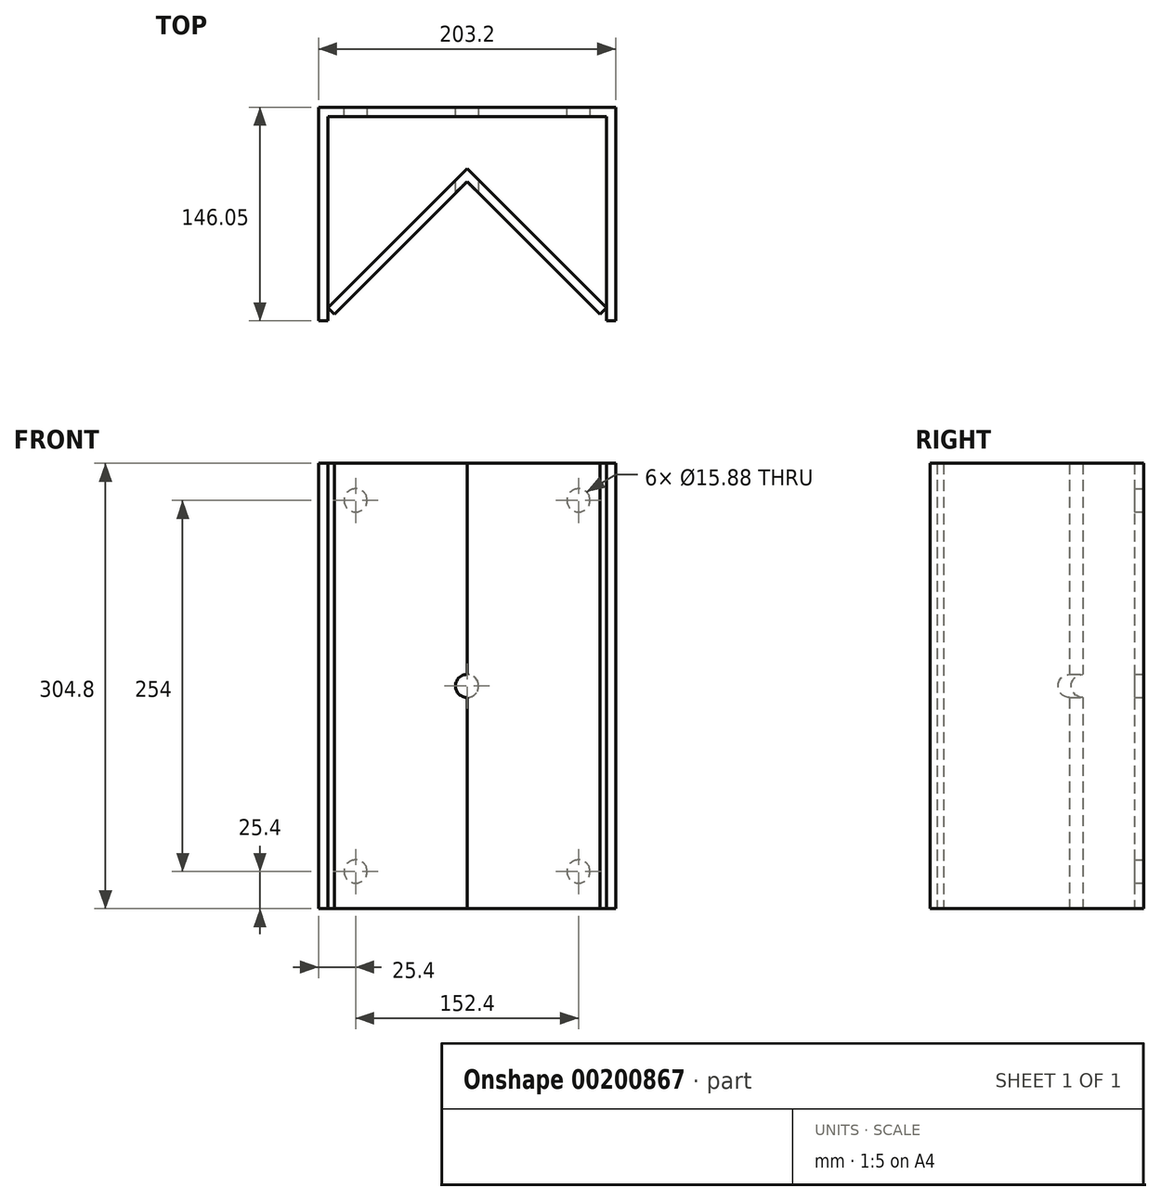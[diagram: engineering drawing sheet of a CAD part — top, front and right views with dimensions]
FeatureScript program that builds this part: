
annotation { "Feature Type Name" : "Feature", "Feature Type Description" : "" }
export const myFeature = defineFeature(function(context is Context, id is Id, definition is map)
    precondition{}
    {
        {
            var Q0;
            Q0=qCreatedBy(makeId("Top.planeOp"),FACE);
            var sketch = newSketch(context, id + "F0", { "sketchPlane" : qUnion([Q0])});
            skLineSegment(sketch, "E0", {"start": v(-95.25, 0) * mm, "end": v(95.25, 0) * mm});
            skLineSegment(sketch, "E1", {"start": v(95.25, 0) * mm, "end": v(95.25, -139.7) * mm});
            skLineSegment(sketch, "E2", {"start": v(95.25, -139.7) * mm, "end": v(101.6, -139.7) * mm});
            skLineSegment(sketch, "E3", {"start": v(101.6, -139.7) * mm, "end": v(101.6, 6.35) * mm});
            skLineSegment(sketch, "E4", {"start": v(101.6, 6.35) * mm, "end": v(-101.6, 6.35) * mm});
            skLineSegment(sketch, "E5", {"start": v(-101.6, 6.35) * mm, "end": v(-101.6, -139.7) * mm});
            skLineSegment(sketch, "E6", {"start": v(-101.6, -139.7) * mm, "end": v(-95.25, -139.7) * mm});
            skLineSegment(sketch, "E7", {"start": v(-95.25, -139.7) * mm, "end": v(-95.25, 0) * mm});
            skSolve(sketch);
        }
        {
            var Q0;
            Q0 = qSketchRegion(id + "F0", true);
            extrude(context, id + "F1", {"entities" : qUnion([Q0]), "depth" : 304.8 * mm});
        }
        {
            var Q0;
            Q0=qCreatedBy(makeId("Top.planeOp"),FACE);
            var sketch = newSketch(context, id + "F2", { "sketchPlane" : qUnion([Q0])});
            skLineSegment(sketch, "E8", {"start": v(-95.25, -139.7) * mm, "end": v(0, -44.45) * mm, "construction": true});
            skLineSegment(sketch, "E9", {"start": v(0, -44.45) * mm, "end": v(95.25, -139.7) * mm, "construction": true});
            skSolve(sketch);
        }
        {
            var Q0;
            Q0=qCreatedBy(makeId("Top.planeOp"),FACE);
            var sketch = newSketch(context, id + "F3", { "sketchPlane" : qUnion([Q0])});
            skLineSegment(sketch, "E10", {"start": v(-90.76, -135.2) * mm, "end": v(0, -44.45) * mm});
            skLineSegment(sketch, "E11", {"start": v(0, -44.45) * mm, "end": v(90.76, -135.2) * mm});
            skLineSegment(sketch, "E12", {"start": v(90.76, -135.2) * mm, "end": v(95.25, -130.72) * mm});
            skLineSegment(sketch, "E13", {"start": v(95.25, -130.72) * mm, "end": v(0, -35.47) * mm});
            skLineSegment(sketch, "E14", {"start": v(-95.25, -130.72) * mm, "end": v(-90.76, -135.2) * mm});
            skLineSegment(sketch, "E15", {"start": v(-95.25, -130.72) * mm, "end": v(0, -35.47) * mm});
            skSolve(sketch);
        }
        {
            var Q0;
            Q0 = qSketchRegion(id + "F3", true);
            var Q1;
            Q1=makeQuery(id+"F1.opExtrude","CAP_FACE",FACE,{"disambiguationData":[OSD([sQuery(id+"F0.wireOp",EDGE,"E0"),sQuery(id+"F0.wireOp",EDGE,"E1"),sQuery(id+"F0.wireOp",EDGE,"E2"),sQuery(id+"F0.wireOp",EDGE,"E3"),sQuery(id+"F0.wireOp",EDGE,"E4"),sQuery(id+"F0.wireOp",EDGE,"E5"),sQuery(id+"F0.wireOp",EDGE,"E6"),sQuery(id+"F0.wireOp",EDGE,"E7")])],"isStart":false});
            extrude(context, id + "F4", {"entities" : qUnion([Q0]), "endBound" : BoundingType.UP_TO_SURFACE, "endBoundEntityFace" : qUnion([Q1]), "depth" : 25.4 * mm});
        }
        {
            var Q0;
            Q0=makeQuery(id+"F1.opExtrude","SWEPT_FACE",FACE,{"disambiguationData":[OSD([sQuery(id+"F0.wireOp",EDGE,"E4")])]});
            var sketch = newSketch(context, id + "F5", { "sketchPlane" : qUnion([Q0])});
            skPoint(sketch, "E16", {"position": v(-76.2, 279.4) * mm});
            skPoint(sketch, "E17", {"position": v(76.2, 279.4) * mm});
            skPoint(sketch, "E18", {"position": v(-76.2, 25.4) * mm});
            skPoint(sketch, "E19", {"position": v(76.2, 25.4) * mm});
            skSolve(sketch);
        }
        {
            var Q0;
            Q0=sQuery(id+"F5.wireOp",VERTEX,"E16");
            var Q1;
            Q1=sQuery(id+"F5.wireOp",VERTEX,"E17");
            var Q2;
            Q2=sQuery(id+"F5.wireOp",VERTEX,"E18");
            var Q3;
            Q3=sQuery(id+"F5.wireOp",VERTEX,"E19");
            var Q4;
            Q4=makeQuery(id+"F1.opExtrude","SWEPT_BODY",BODY,{"disambiguationData":[OSD([sQuery(id+"F0.wireOp",EDGE,"E0"),sQuery(id+"F0.wireOp",EDGE,"E1"),sQuery(id+"F0.wireOp",EDGE,"E2"),sQuery(id+"F0.wireOp",EDGE,"E3"),sQuery(id+"F0.wireOp",EDGE,"E4"),sQuery(id+"F0.wireOp",EDGE,"E5"),sQuery(id+"F0.wireOp",EDGE,"E6"),sQuery(id+"F0.wireOp",EDGE,"E7")])]});
            var Q5;
            Q5=makeQuery(id+"F4.opExtrude","SWEPT_BODY",BODY,{"disambiguationData":[OSD([sQuery(id+"F3.wireOp",EDGE,"E10"),sQuery(id+"F3.wireOp",EDGE,"E11"),sQuery(id+"F3.wireOp",EDGE,"E12"),sQuery(id+"F3.wireOp",EDGE,"E13"),sQuery(id+"F3.wireOp",EDGE,"E14"),sQuery(id+"F3.wireOp",EDGE,"E15")])]});
            hole(context, id + "F6", {"style" : HoleStyle.SIMPLE, "endStyle" : HoleEndStyle.BLIND, "holeDiameter" : 15.88 * mm, "holeDepth" : 12.7 * mm, "locations" : qUnion([Q0, Q1, Q2, Q3]), "scope" : qUnion([Q4, Q5])});
        }
        {
            var Q0;
            Q0=makeQuery(id+"F1.opExtrude","SWEPT_FACE",FACE,{"disambiguationData":[OSD([sQuery(id+"F0.wireOp",EDGE,"E4")])]});
            var sketch = newSketch(context, id + "F7", { "sketchPlane" : qUnion([Q0])});
            skLineSegment(sketch, "E20", {"start": v(-101.6, 304.8) * mm, "end": v(101.6, 0) * mm, "construction": true});
            skPoint(sketch, "E21", {"position": v(0, 152.4) * mm});
            skSolve(sketch);
        }
        {
            var Q0;
            Q0=sQuery(id+"F7.wireOp",VERTEX,"E21");
            var Q1;
            Q1=makeQuery(id+"F1.opExtrude","SWEPT_BODY",BODY,{"disambiguationData":[OSD([sQuery(id+"F0.wireOp",EDGE,"E0"),sQuery(id+"F0.wireOp",EDGE,"E1"),sQuery(id+"F0.wireOp",EDGE,"E2"),sQuery(id+"F0.wireOp",EDGE,"E3"),sQuery(id+"F0.wireOp",EDGE,"E4"),sQuery(id+"F0.wireOp",EDGE,"E5"),sQuery(id+"F0.wireOp",EDGE,"E6"),sQuery(id+"F0.wireOp",EDGE,"E7")])]});
            var Q2;
            Q2=makeQuery(id+"F4.opExtrude","SWEPT_BODY",BODY,{"disambiguationData":[OSD([sQuery(id+"F3.wireOp",EDGE,"E10"),sQuery(id+"F3.wireOp",EDGE,"E11"),sQuery(id+"F3.wireOp",EDGE,"E12"),sQuery(id+"F3.wireOp",EDGE,"E13"),sQuery(id+"F3.wireOp",EDGE,"E14"),sQuery(id+"F3.wireOp",EDGE,"E15")])]});
            hole(context, id + "F8", {"style" : HoleStyle.SIMPLE, "endStyle" : HoleEndStyle.THROUGH, "holeDiameter" : 15.88 * mm, "locations" : qUnion([Q0]), "scope" : qUnion([Q1, Q2]), "isTappedThrough" : true});
        }
    });
